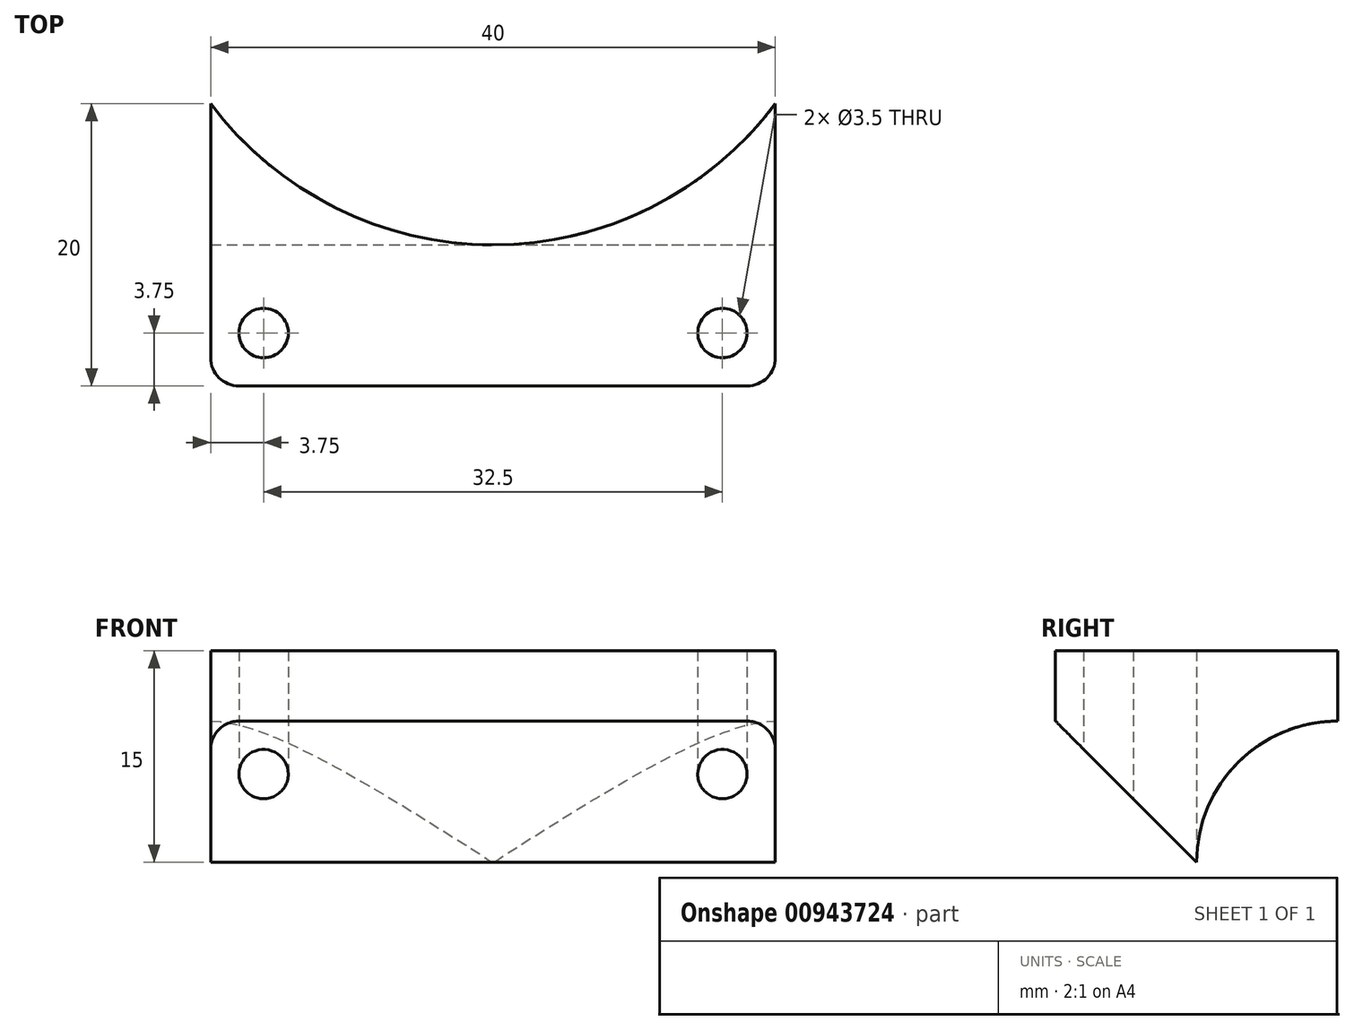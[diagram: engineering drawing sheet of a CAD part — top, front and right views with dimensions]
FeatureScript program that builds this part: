
annotation { "Feature Type Name" : "Feature", "Feature Type Description" : "" }
export const myFeature = defineFeature(function(context is Context, id is Id, definition is map)
    precondition{}
    {
        {
            var Q0;
            Q0=qCreatedBy(makeId("Top.planeOp"),FACE);
            var sketch = newSketch(context, id + "F0", { "sketchPlane" : qUnion([Q0])});
            skLineSegment(sketch, "E0.bottom", {"start": v(-20, 10) * mm, "end": v(20, 10) * mm});
            skLineSegment(sketch, "E0.top", {"start": v(-18, -10) * mm, "end": v(18, -10) * mm});
            skLineSegment(sketch, "E0.left", {"start": v(-20, 10) * mm, "end": v(-20, -8) * mm});
            skLineSegment(sketch, "E0.right", {"start": v(20, 10) * mm, "end": v(20, -8) * mm});
            skPoint(sketch, "E0.middle", {"position": v(0, 0) * mm});
            skCircle(sketch, "E1", {"center": v(0, 25) * mm, "radius": 25 * mm});
            skCircle(sketch, "E2", {"center": v(-16.25, -6.25) * mm, "radius": 1.75 * mm});
            skCircle(sketch, "E3.MirrorC", {"center": v(16.25, -6.25) * mm, "radius": 1.75 * mm});
            skPoint(sketch, "E4.visualSharp", {"position": v(-20, -10) * mm});
            skArc(sketch, "E4.filletArc", {"start": v(-20, -8) * mm, "mid": v(-19.41, -9.41) * mm, "end": v(-18, -10) * mm});
            skPoint(sketch, "E5.visualSharp", {"position": v(20, -10) * mm});
            skArc(sketch, "E5.filletArc", {"start": v(18, -10) * mm, "mid": v(19.41, -9.41) * mm, "end": v(20, -8) * mm});
            skSolve(sketch);
        }
        {
            var Q0;
            Q0=makeQuery(id+"F0.imprint","IMPRINT",FACE,{"disambiguationData":[TD([[makeQuery(id+"F0.imprint","IMPRINT",EDGE,{"derivedFrom":sQuery(id+"F0.wireOp",EDGE,"E0.top")}),1.0]])]});
            extrude(context, id + "F1", {"entities" : qUnion([Q0]), "depth" : 15 * mm, "offsetDistance" : 25 * mm});
        }
        {
            var Q0;
            Q0=qCreatedBy(makeId("Right.planeOp"),FACE);
            var sketch = newSketch(context, id + "F2", { "sketchPlane" : qUnion([Q0])});
            skCircle(sketch, "E6", {"center": v(10, 0) * mm, "radius": 10 * mm});
            skLineSegment(sketch, "E7", {"start": v(-10, 0) * mm, "end": v(-10, 10) * mm});
            skLineSegment(sketch, "E8", {"start": v(-10, 10) * mm, "end": v(0, 0) * mm});
            skLineSegment(sketch, "E9", {"start": v(0, 0) * mm, "end": v(-10, 0) * mm});
            skSolve(sketch);
        }
        {
            var Q0;
            Q0 = qSketchRegion(id + "F2", true);
            extrude(context, id + "F3", {"entities" : qUnion([Q0]), "operationType" : NewBodyOperationType.REMOVE, "oppositeDirection" : true, "depth" : 25 * mm, "offsetDistance" : 25 * mm, "hasSecondDirection" : true, "secondDirectionOppositeDirection" : false, "secondDirectionDepth" : 25 * mm});
        }
    });
